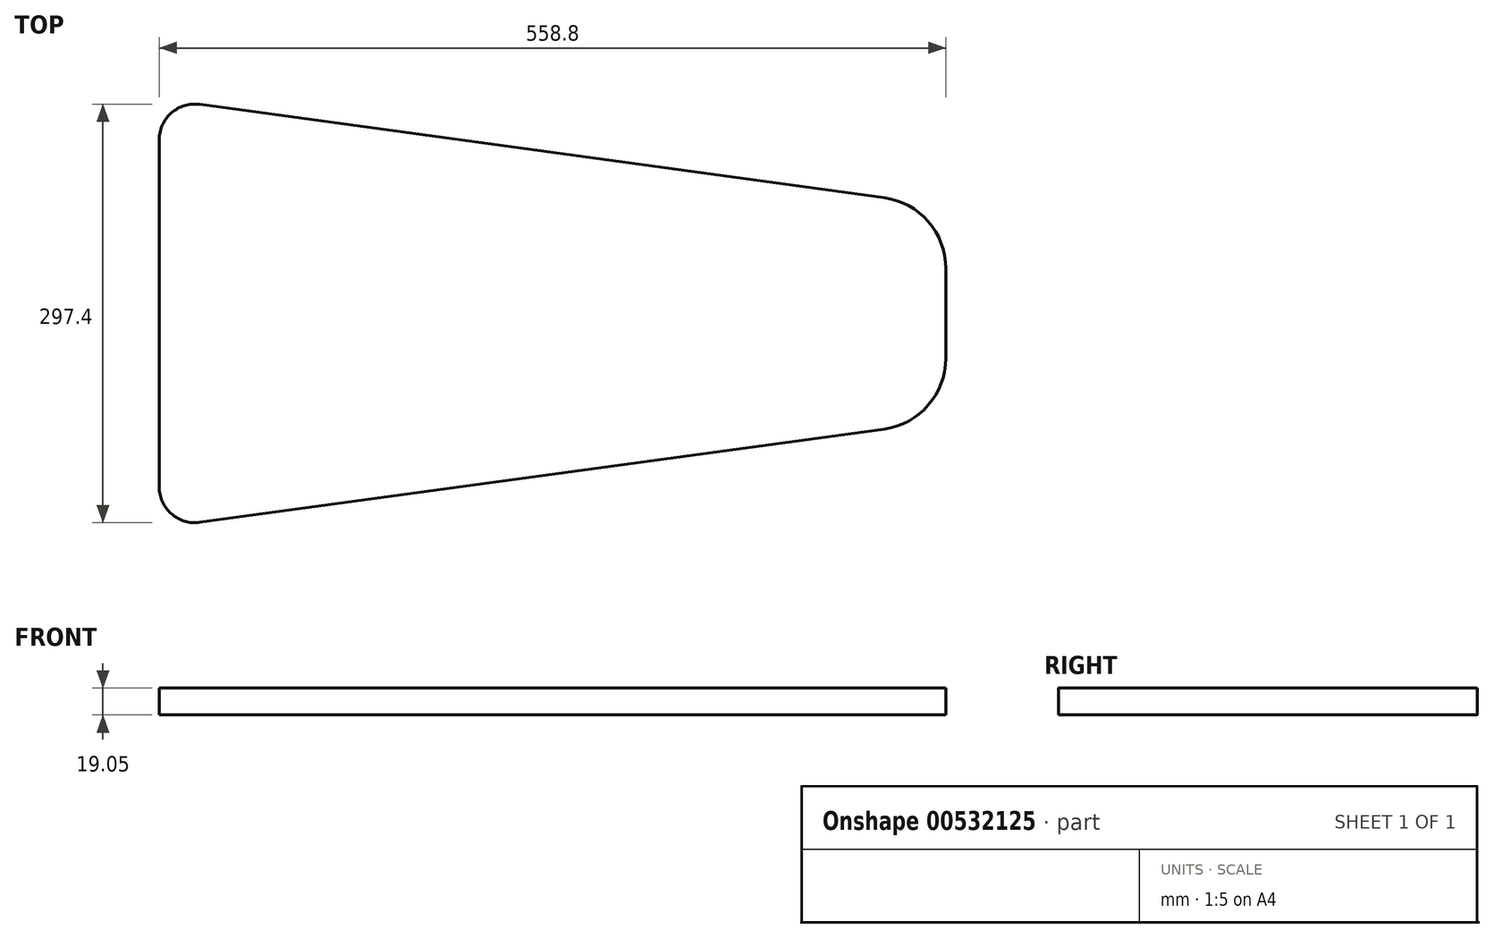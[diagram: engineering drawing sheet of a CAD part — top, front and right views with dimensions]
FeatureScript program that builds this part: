
annotation { "Feature Type Name" : "Feature", "Feature Type Description" : "" }
export const myFeature = defineFeature(function(context is Context, id is Id, definition is map)
    precondition{}
    {
        {
            var Q0;
            Q0=qCreatedBy(makeId("Top.planeOp"),FACE);
            var sketch = newSketch(context, id + "F0", { "sketchPlane" : qUnion([Q0])});
            skLineSegment(sketch, "E0", {"start": v(-279.4, 123.3) * mm, "end": v(-279.4, -123.3) * mm});
            skLineSegment(sketch, "E1", {"start": v(-250.57, 148.47) * mm, "end": v(235.46, 82.2) * mm});
            skLineSegment(sketch, "E2", {"start": v(279.4, -31.86) * mm, "end": v(279.4, 31.86) * mm});
            skLineSegment(sketch, "E3", {"start": v(235.46, -82.2) * mm, "end": v(-250.57, -148.47) * mm});
            skLineSegment(sketch, "E4", {"start": v(-279.4, 0) * mm, "end": v(279.4, 0) * mm, "construction": true});
            skPoint(sketch, "E5", {"position": v(0, 0) * mm});
            skPoint(sketch, "E6.visualSharp", {"position": v(-279.4, 152.4) * mm});
            skArc(sketch, "E6.filletArc", {"start": v(-250.57, 148.47) * mm, "mid": v(-270.7, 142.44) * mm, "end": v(-279.4, 123.3) * mm});
            skPoint(sketch, "E7.visualSharp", {"position": v(-279.4, -152.4) * mm});
            skArc(sketch, "E7.filletArc", {"start": v(-279.4, -123.3) * mm, "mid": v(-270.7, -142.44) * mm, "end": v(-250.57, -148.47) * mm});
            skPoint(sketch, "E8.visualSharp", {"position": v(279.4, -76.2) * mm});
            skArc(sketch, "E8.filletArc", {"start": v(235.46, -82.2) * mm, "mid": v(266.87, -65.26) * mm, "end": v(279.4, -31.86) * mm});
            skPoint(sketch, "E9.visualSharp", {"position": v(279.4, 76.2) * mm});
            skArc(sketch, "E9.filletArc", {"start": v(279.4, 31.86) * mm, "mid": v(266.87, 65.26) * mm, "end": v(235.46, 82.2) * mm});
            skSolve(sketch);
        }
        {
            var Q0;
            Q0 = qSketchRegion(id + "F0", true);
            extrude(context, id + "F1", {"entities" : qUnion([Q0]), "depth" : 19.05 * mm, "offsetDistance" : 25.4 * mm});
        }
    });
